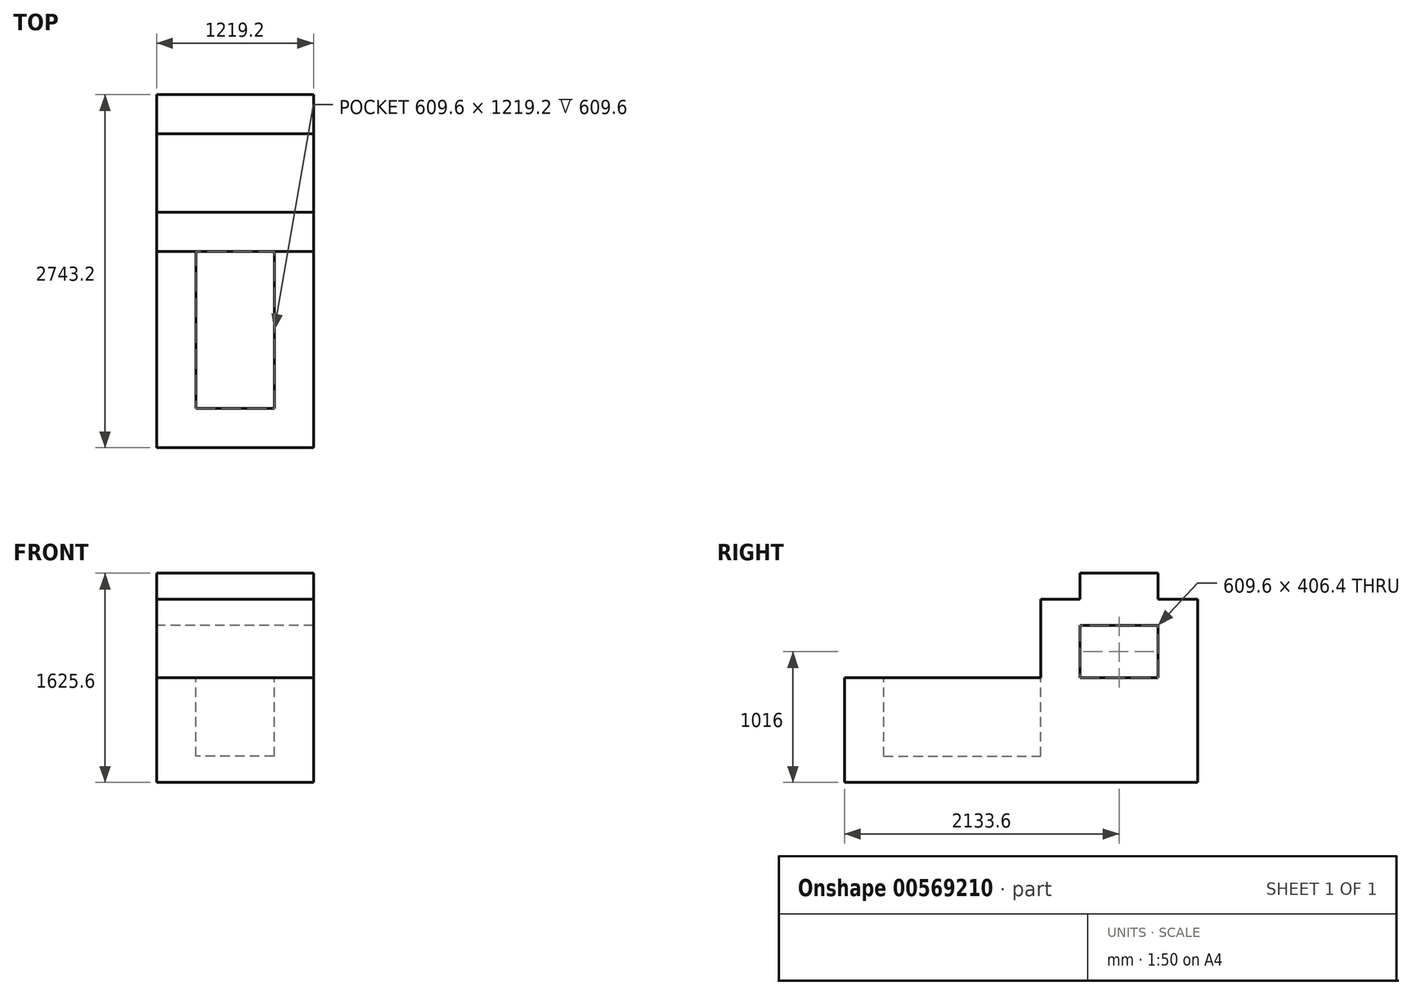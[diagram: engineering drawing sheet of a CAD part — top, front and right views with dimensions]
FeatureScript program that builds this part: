
annotation { "Feature Type Name" : "Feature", "Feature Type Description" : "" }
export const myFeature = defineFeature(function(context is Context, id is Id, definition is map)
    precondition{}
    {
        {
            var Q0;
            Q0=qCreatedBy(makeId("Right.planeOp"),FACE);
            var sketch = newSketch(context, id + "F0", { "sketchPlane" : qUnion([Q0])});
            skLineSegment(sketch, "E0", {"start": v(0, 0) * mm, "end": v(2743.2, 0) * mm});
            skLineSegment(sketch, "E1", {"start": v(2743.2, 0) * mm, "end": v(2743.2, 1422.4) * mm});
            skLineSegment(sketch, "E2", {"start": v(2743.2, 1422.4) * mm, "end": v(2438.4, 1422.4) * mm});
            skLineSegment(sketch, "E3", {"start": v(2438.4, 1422.4) * mm, "end": v(2438.4, 1625.6) * mm});
            skLineSegment(sketch, "E4", {"start": v(2438.4, 1625.6) * mm, "end": v(1828.8, 1625.6) * mm});
            skLineSegment(sketch, "E5", {"start": v(1828.8, 1625.6) * mm, "end": v(1828.8, 1422.4) * mm});
            skLineSegment(sketch, "E6", {"start": v(1828.8, 1422.4) * mm, "end": v(1524, 1422.4) * mm});
            skLineSegment(sketch, "E7", {"start": v(1524, 1422.4) * mm, "end": v(1524, 812.8) * mm});
            skLineSegment(sketch, "E8", {"start": v(1524, 812.8) * mm, "end": v(0, 812.8) * mm});
            skLineSegment(sketch, "E9", {"start": v(0, 812.8) * mm, "end": v(0, 0) * mm});
            skLineSegment(sketch, "E10", {"start": v(1828.8, 1219.2) * mm, "end": v(2438.4, 1219.2) * mm});
            skLineSegment(sketch, "E11", {"start": v(2438.4, 1219.2) * mm, "end": v(2438.4, 812.8) * mm});
            skLineSegment(sketch, "E12", {"start": v(2438.4, 812.8) * mm, "end": v(1828.8, 812.8) * mm});
            skLineSegment(sketch, "E13", {"start": v(1828.8, 812.8) * mm, "end": v(1828.8, 1219.2) * mm});
            skSolve(sketch);
        }
        {
            var Q0;
            Q0 = qSketchRegion(id + "F0", true);
            extrude(context, id + "F1", {"entities" : qUnion([Q0]), "depth" : 1219.2 * mm, "offsetDistance" : 25.4 * mm});
        }
        {
            var Q0;
            Q0=qCreatedBy(makeId("Top.planeOp"),FACE);
            var sketch = newSketch(context, id + "F2", { "sketchPlane" : qUnion([Q0])});
            skLineSegment(sketch, "E14", {"start": v(304.8, 203.2) * mm, "end": v(304.8, 1422.4) * mm});
            skLineSegment(sketch, "E15", {"start": v(304.8, 1422.4) * mm, "end": v(914.4, 1422.4) * mm});
            skLineSegment(sketch, "E16", {"start": v(914.4, 1422.4) * mm, "end": v(914.4, 203.2) * mm});
            skLineSegment(sketch, "E17", {"start": v(914.4, 203.2) * mm, "end": v(304.8, 203.2) * mm});
            skSolve(sketch);
        }
        {
            var Q0;
            Q0=makeQuery(id+"F2.imprint","IMPRINT",FACE,{"disambiguationData":[TD([[makeQuery(id+"F2.imprint","IMPRINT",EDGE,{"derivedFrom":sQuery(id+"F2.wireOp",EDGE,"E14")}),-1.0]])]});
            extrude(context, id + "F3", {"entities" : qUnion([Q0]), "operationType" : NewBodyOperationType.ADD, "depth" : 609.6 * mm, "offsetDistance" : 25.4 * mm});
        }
        {
            var Q0;
            Q0=makeQuery(id+"F1.opExtrude","SWEPT_FACE",FACE,{"disambiguationData":[OSD([sQuery(id+"F0.wireOp",EDGE,"E8")])]});
            var sketch = newSketch(context, id + "F4", { "sketchPlane" : qUnion([Q0])});
            skLineSegment(sketch, "E18", {"start": v(304.8, 304.8) * mm, "end": v(304.8, 1524) * mm});
            skLineSegment(sketch, "E19", {"start": v(304.8, 1524) * mm, "end": v(914.4, 1524) * mm});
            skLineSegment(sketch, "E20", {"start": v(914.4, 1524) * mm, "end": v(914.4, 304.8) * mm});
            skLineSegment(sketch, "E21", {"start": v(914.4, 304.8) * mm, "end": v(304.8, 304.8) * mm});
            skSolve(sketch);
        }
        {
            var Q0;
            Q0=makeQuery(id+"F4.imprint","IMPRINT",FACE,{"disambiguationData":[TD([[makeQuery(id+"F4.imprint","IMPRINT",EDGE,{"derivedFrom":sQuery(id+"F4.wireOp",EDGE,"E18")}),-1.0]])]});
            extrude(context, id + "F5", {"entities" : qUnion([Q0]), "operationType" : NewBodyOperationType.REMOVE, "oppositeDirection" : true, "depth" : 609.6 * mm, "offsetDistance" : 25.4 * mm});
        }
    });
